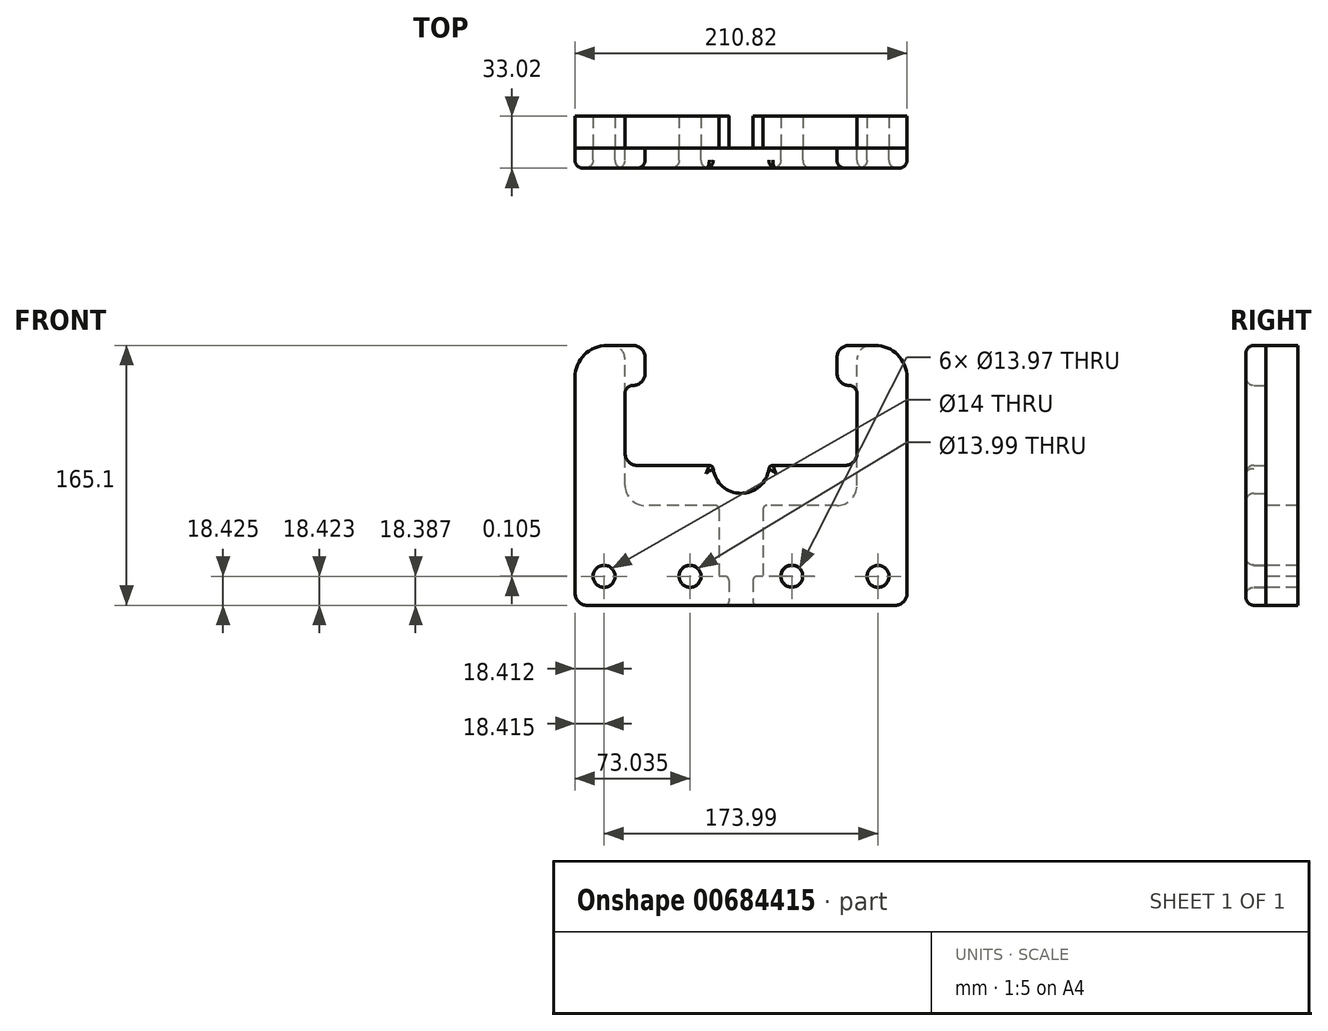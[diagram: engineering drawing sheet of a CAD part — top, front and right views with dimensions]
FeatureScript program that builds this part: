
annotation { "Feature Type Name" : "Feature", "Feature Type Description" : "" }
export const myFeature = defineFeature(function(context is Context, id is Id, definition is map)
    precondition{}
    {
        {
            var Q0;
            Q0=qCreatedBy(makeId("Front.planeOp"),FACE);
            var sketch = newSketch(context, id + "F0", { "sketchPlane" : qUnion([Q0])});
            skLineSegment(sketch, "E0.bottom", {"start": v(53.34, -100.21) * mm, "end": v(8.89, -100.21) * mm});
            skLineSegment(sketch, "E0.left", {"start": v(66.04, -87.51) * mm, "end": v(66.04, -7.5) * mm});
            skLineSegment(sketch, "E0.right", {"start": v(-81.28, -87.51) * mm, "end": v(-81.28, -7.5) * mm});
            skPoint(sketch, "E0.middle", {"position": v(-7.62, 44.57) * mm});
            skPoint(sketch, "E1.visualSharp", {"position": v(-81.28, -100.21) * mm});
            skArc(sketch, "E1.filletArc", {"start": v(-81.28, -87.51) * mm, "mid": v(-77.56, -96.5) * mm, "end": v(-68.58, -100.21) * mm});
            skPoint(sketch, "E2.visualSharp", {"position": v(66.04, -100.21) * mm});
            skArc(sketch, "E2.filletArc", {"start": v(53.34, -100.21) * mm, "mid": v(62.32, -96.5) * mm, "end": v(66.04, -87.51) * mm});
            skPoint(sketch, "E3.visualSharp", {"position": v(66.04, 189.35) * mm});
            skPoint(sketch, "E4.visualSharp", {"position": v(-81.28, 189.35) * mm});
            skLineSegment(sketch, "E5", {"start": v(-92.71, 1.39) * mm, "end": v(-90.17, 1.39) * mm});
            skLineSegment(sketch, "E6", {"start": v(-113.03, -18.93) * mm, "end": v(-113.03, -156.1) * mm});
            skLineSegment(sketch, "E7", {"start": v(97.79, -18.93) * mm, "end": v(97.79, -156.1) * mm});
            skLineSegment(sketch, "E8", {"start": v(-105.41, -163.71) * mm, "end": v(-17.78, -163.71) * mm});
            skLineSegment(sketch, "E9.trimOffspring", {"start": v(74.93, 1.39) * mm, "end": v(77.47, 1.39) * mm});
            skPoint(sketch, "E10.visualSharp", {"position": v(-113.03, 1.39) * mm});
            skArc(sketch, "E10.filletArc", {"start": v(-92.71, 1.39) * mm, "mid": v(-107.08, -4.57) * mm, "end": v(-113.03, -18.93) * mm});
            skPoint(sketch, "E11.visualSharp", {"position": v(-81.28, 1.39) * mm});
            skArc(sketch, "E11.filletArc", {"start": v(-81.28, -7.5) * mm, "mid": v(-83.88, -1.22) * mm, "end": v(-90.17, 1.39) * mm});
            skPoint(sketch, "E12.visualSharp", {"position": v(66.04, 1.39) * mm});
            skArc(sketch, "E12.filletArc", {"start": v(74.93, 1.39) * mm, "mid": v(68.64, -1.22) * mm, "end": v(66.04, -7.5) * mm});
            skPoint(sketch, "E13.visualSharp", {"position": v(97.79, 1.39) * mm});
            skArc(sketch, "E13.filletArc", {"start": v(97.79, -18.93) * mm, "mid": v(91.84, -4.57) * mm, "end": v(77.47, 1.39) * mm});
            skLineSegment(sketch, "E14", {"start": v(-21.6, -100.21) * mm, "end": v(-21.6, -145.3) * mm});
            skLineSegment(sketch, "E15", {"start": v(-21.6, -145.3) * mm, "end": v(-21.6, -102.75) * mm});
            skLineSegment(sketch, "E16", {"start": v(6.35, -102.75) * mm, "end": v(6.35, -145.3) * mm});
            skLineSegment(sketch, "E17", {"start": v(6.35, -145.3) * mm, "end": v(2.54, -145.3) * mm});
            skLineSegment(sketch, "E18", {"start": v(0, -147.84) * mm, "end": v(0, -161.17) * mm});
            skLineSegment(sketch, "E19", {"start": v(0, -163.71) * mm, "end": v(0, -147.84) * mm});
            skLineSegment(sketch, "E20", {"start": v(-15.24, -147.84) * mm, "end": v(-15.24, -161.17) * mm});
            skLineSegment(sketch, "E21.trimOffspring", {"start": v(-24.13, -100.21) * mm, "end": v(-68.58, -100.21) * mm});
            skPoint(sketch, "E22.visualSharp", {"position": v(-21.6, -100.21) * mm});
            skArc(sketch, "E22.filletArc", {"start": v(-21.6, -102.75) * mm, "mid": v(-22.33, -100.96) * mm, "end": v(-24.13, -100.21) * mm});
            skPoint(sketch, "E23.visualSharp", {"position": v(6.35, -100.21) * mm});
            skArc(sketch, "E23.filletArc", {"start": v(8.89, -100.21) * mm, "mid": v(7.1, -100.96) * mm, "end": v(6.35, -102.75) * mm});
            skLineSegment(sketch, "E24.trimOffspring", {"start": v(-17.78, -145.3) * mm, "end": v(-21.6, -145.3) * mm});
            skLineSegment(sketch, "E25.trimOffspring", {"start": v(2.54, -163.71) * mm, "end": v(90.17, -163.71) * mm});
            skPoint(sketch, "E26.visualSharp", {"position": v(-15.24, -145.3) * mm});
            skArc(sketch, "E26.filletArc", {"start": v(-15.24, -147.84) * mm, "mid": v(-15.98, -146.04) * mm, "end": v(-17.78, -145.3) * mm});
            skPoint(sketch, "E27.visualSharp", {"position": v(0, -145.3) * mm});
            skArc(sketch, "E27.filletArc", {"start": v(2.54, -145.3) * mm, "mid": v(0.74, -146.04) * mm, "end": v(0, -147.84) * mm});
            skPoint(sketch, "E28.visualSharp", {"position": v(0, -163.71) * mm});
            skArc(sketch, "E28.filletArc", {"start": v(0, -161.17) * mm, "mid": v(0.74, -162.97) * mm, "end": v(2.54, -163.71) * mm});
            skPoint(sketch, "E29.visualSharp", {"position": v(-15.24, -163.71) * mm});
            skArc(sketch, "E29.filletArc", {"start": v(-17.78, -163.71) * mm, "mid": v(-15.98, -162.97) * mm, "end": v(-15.24, -161.17) * mm});
            skLineSegment(sketch, "E30", {"start": v(-21.6, -145.3) * mm, "end": v(-17.78, -145.3) * mm});
            skCircle(sketch, "E31", {"center": v(-94.62, -145.3) * mm, "radius": 6.99 * mm});
            skCircle(sketch, "E32", {"center": v(-40, -145.3) * mm, "radius": 6.99 * mm});
            skCircle(sketch, "E33", {"center": v(24.76, -145.3) * mm, "radius": 6.99 * mm});
            skCircle(sketch, "E34", {"center": v(79.37, -145.3) * mm, "radius": 6.99 * mm});
            skPoint(sketch, "E35.orphan", {"position": v(-113.03, -145.3) * mm});
            skPoint(sketch, "E36.trimOffspring.end.orphan", {"position": v(-94.62, -163.71) * mm});
            skPoint(sketch, "E37.start.orphan", {"position": v(-40, -163.71) * mm});
            skLineSegment(sketch, "E38.trimOffspring", {"start": v(2.54, -145.3) * mm, "end": v(6.35, -145.3) * mm});
            skPoint(sketch, "E39.start.orphan", {"position": v(24.77, -163.71) * mm});
            skPoint(sketch, "E40.orphan", {"position": v(79.37, -163.71) * mm});
            skPoint(sketch, "E41.visualSharp", {"position": v(-113.03, -163.71) * mm});
            skArc(sketch, "E41.filletArc", {"start": v(-113.03, -156.1) * mm, "mid": v(-110.8, -161.48) * mm, "end": v(-105.41, -163.71) * mm});
            skPoint(sketch, "E42.visualSharp", {"position": v(97.79, -163.71) * mm});
            skArc(sketch, "E42.filletArc", {"start": v(90.17, -163.71) * mm, "mid": v(95.56, -161.48) * mm, "end": v(97.79, -156.1) * mm});
            skSolve(sketch);
        }
        {
            var Q0;
            Q0=makeQuery(id+"F0.imprint","IMPRINT",FACE,{"disambiguationData":[TD([[makeQuery(id+"F0.imprint","IMPRINT",EDGE,{"derivedFrom":sQuery(id+"F0.wireOp",EDGE,"E0.right")}),1.0]])]});
            var sketch = newSketch(context, id + "F1", { "sketchPlane" : qUnion([Q0])});
            skLineSegment(sketch, "E43.0", {"start": v(-81.28, -67.2) * mm, "end": v(-81.28, -29.1) * mm});
            skArc(sketch, "E43.7", {"start": v(-92.71, 1.39) * mm, "mid": v(-107.08, -4.57) * mm, "end": v(-113.03, -18.93) * mm});
            skLineSegment(sketch, "E43.8", {"start": v(-113.03, -18.93) * mm, "end": v(-113.03, -156.1) * mm});
            skLineSegment(sketch, "E43.9", {"start": v(-105.41, -163.71) * mm, "end": v(-15.24, -163.71) * mm});
            skArc(sketch, "E44.1", {"start": v(97.79, -18.93) * mm, "mid": v(91.84, -4.57) * mm, "end": v(77.47, 1.39) * mm});
            skLineSegment(sketch, "E44.2", {"start": v(97.79, -156.1) * mm, "end": v(97.79, -18.93) * mm});
            skLineSegment(sketch, "E44.3", {"start": v(0, -163.71) * mm, "end": v(90.17, -163.71) * mm});
            skLineSegment(sketch, "E44.6", {"start": v(66.04, -29.1) * mm, "end": v(66.04, -67.2) * mm});
            skLineSegment(sketch, "E45", {"start": v(-56.44, -74.81) * mm, "end": v(-27.78, -74.81) * mm});
            skLineSegment(sketch, "E46", {"start": v(-56.44, -74.81) * mm, "end": v(-73.66, -74.81) * mm});
            skLineSegment(sketch, "E47", {"start": v(-15.24, -163.71) * mm, "end": v(0, -163.71) * mm});
            skPoint(sketch, "E48.orphan", {"position": v(-58.21, 0) * mm});
            skLineSegment(sketch, "E49", {"start": v(-92.71, 1.39) * mm, "end": v(-76.2, 1.39) * mm});
            skLineSegment(sketch, "E50", {"start": v(77.47, 1.39) * mm, "end": v(60.96, 1.39) * mm});
            skLineSegment(sketch, "E51", {"start": v(-68.58, -6.23) * mm, "end": v(-68.58, -16.4) * mm});
            skLineSegment(sketch, "E52", {"start": v(53.34, -6.23) * mm, "end": v(53.34, -16.4) * mm});
            skLineSegment(sketch, "E53", {"start": v(60.96, -24.01) * mm, "end": v(60.96, -24.01) * mm});
            skLineSegment(sketch, "E54", {"start": v(-76.2, -24.01) * mm, "end": v(-76.2, -24.01) * mm});
            skPoint(sketch, "E55.visualSharp", {"position": v(-68.58, 1.39) * mm});
            skArc(sketch, "E55.filletArc", {"start": v(-68.58, -6.23) * mm, "mid": v(-70.81, -0.85) * mm, "end": v(-76.2, 1.39) * mm});
            skPoint(sketch, "E56.visualSharp", {"position": v(-68.58, -24.01) * mm});
            skArc(sketch, "E56.filletArc", {"start": v(-76.2, -24.01) * mm, "mid": v(-70.81, -21.78) * mm, "end": v(-68.58, -16.4) * mm});
            skPoint(sketch, "E57.newPointB", {"position": v(-81.28, -7.5) * mm});
            skArc(sketch, "E57.filletArc", {"start": v(-76.2, -24.01) * mm, "mid": v(-79.8, -25.5) * mm, "end": v(-81.28, -29.1) * mm});
            skPoint(sketch, "E58.visualSharp", {"position": v(53.34, 1.39) * mm});
            skArc(sketch, "E58.filletArc", {"start": v(60.96, 1.39) * mm, "mid": v(55.57, -0.85) * mm, "end": v(53.34, -6.23) * mm});
            skPoint(sketch, "E59.orphan", {"position": v(66.04, -7.5) * mm});
            skPoint(sketch, "E60.visualSharp", {"position": v(53.34, -24.01) * mm});
            skArc(sketch, "E60.filletArc", {"start": v(53.34, -16.4) * mm, "mid": v(55.57, -21.78) * mm, "end": v(60.96, -24.01) * mm});
            skPoint(sketch, "E61.visualSharp", {"position": v(66.04, -24.01) * mm});
            skArc(sketch, "E61.filletArc", {"start": v(66.04, -29.1) * mm, "mid": v(64.55, -25.5) * mm, "end": v(60.96, -24.01) * mm});
            skPoint(sketch, "E62.visualSharp", {"position": v(-81.28, -74.81) * mm});
            skArc(sketch, "E62.filletArc", {"start": v(-81.28, -67.2) * mm, "mid": v(-79.05, -72.58) * mm, "end": v(-73.66, -74.81) * mm});
            skPoint(sketch, "E63.visualSharp", {"position": v(66.04, -74.81) * mm});
            skArc(sketch, "E63.filletArc", {"start": v(58.42, -74.81) * mm, "mid": v(63.8, -72.58) * mm, "end": v(66.04, -67.2) * mm});
            skPoint(sketch, "E64", {"position": v(-7.62, -74.81) * mm});
            skArc(sketch, "E65", {"start": v(-25.26, -77.04) * mm, "mid": v(-7.62, -92.6) * mm, "end": v(10.02, -77.04) * mm});
            skLineSegment(sketch, "E66.trimOffspring", {"start": v(12.54, -74.81) * mm, "end": v(58.42, -74.81) * mm});
            skPoint(sketch, "E67.visualSharp", {"position": v(-25.4, -74.81) * mm});
            skArc(sketch, "E67.filletArc", {"start": v(-25.26, -77.04) * mm, "mid": v(-26.1, -75.45) * mm, "end": v(-27.78, -74.81) * mm});
            skPoint(sketch, "E68.visualSharp", {"position": v(10.16, -74.81) * mm});
            skArc(sketch, "E68.filletArc", {"start": v(12.54, -74.81) * mm, "mid": v(10.86, -75.45) * mm, "end": v(10.02, -77.04) * mm});
            skPoint(sketch, "E69.visualSharp", {"position": v(-113.03, -163.71) * mm});
            skArc(sketch, "E69.filletArc", {"start": v(-113.03, -156.1) * mm, "mid": v(-110.8, -161.48) * mm, "end": v(-105.41, -163.71) * mm});
            skPoint(sketch, "E70.visualSharp", {"position": v(97.79, -163.71) * mm});
            skArc(sketch, "E70.filletArc", {"start": v(90.17, -163.71) * mm, "mid": v(95.56, -161.48) * mm, "end": v(97.79, -156.1) * mm});
            skCircle(sketch, "E71", {"center": v(24.62, -145.22) * mm, "radius": 6.99 * mm});
            skCircle(sketch, "E72", {"center": v(79.37, -145.32) * mm, "radius": 6.99 * mm});
            skCircle(sketch, "E73", {"center": v(-94.62, -145.29) * mm, "radius": 7 * mm});
            skCircle(sketch, "E74", {"center": v(-40, -145.28) * mm, "radius": 7 * mm});
            skSolve(sketch);
        }
        {
            var Q0;
            Q0 = qSketchRegion(id + "F0", true);
            extrude(context, id + "F2", {"entities" : qUnion([Q0]), "depth" : -20.32 * mm, "offsetDistance" : 25.4 * mm});
        }
        {
            var Q0;
            Q0 = qSketchRegion(id + "F1", true);
            extrude(context, id + "F3", {"entities" : qUnion([Q0]), "depth" : 12.7 * mm, "offsetDistance" : 25.4 * mm});
        }
        {
            var Q0;
            Q0=makeQuery(id+"F3.opExtrude","CAP_FACE",FACE,{"disambiguationData":[OSD([sQuery(id+"F1.wireOp",EDGE,"E43.0"),sQuery(id+"F1.wireOp",EDGE,"E43.7"),sQuery(id+"F1.wireOp",EDGE,"E43.8"),sQuery(id+"F1.wireOp",EDGE,"E43.9"),sQuery(id+"F1.wireOp",EDGE,"E44.1"),sQuery(id+"F1.wireOp",EDGE,"E44.2"),sQuery(id+"F1.wireOp",EDGE,"E44.3"),sQuery(id+"F1.wireOp",EDGE,"E44.6"),sQuery(id+"F1.wireOp",EDGE,"E45"),sQuery(id+"F1.wireOp",EDGE,"E46"),sQuery(id+"F1.wireOp",EDGE,"E47"),sQuery(id+"F1.wireOp",EDGE,"E49"),sQuery(id+"F1.wireOp",EDGE,"E50"),sQuery(id+"F1.wireOp",EDGE,"E51"),sQuery(id+"F1.wireOp",EDGE,"E52"),sQuery(id+"F1.wireOp",EDGE,"E55.filletArc"),sQuery(id+"F1.wireOp",EDGE,"E56.filletArc"),sQuery(id+"F1.wireOp",EDGE,"E57.filletArc"),sQuery(id+"F1.wireOp",EDGE,"E58.filletArc"),sQuery(id+"F1.wireOp",EDGE,"E60.filletArc"),sQuery(id+"F1.wireOp",EDGE,"E61.filletArc"),sQuery(id+"F1.wireOp",EDGE,"E62.filletArc"),sQuery(id+"F1.wireOp",EDGE,"E63.filletArc"),sQuery(id+"F1.wireOp",EDGE,"E65"),sQuery(id+"F1.wireOp",EDGE,"E66.trimOffspring"),sQuery(id+"F1.wireOp",EDGE,"E67.filletArc"),sQuery(id+"F1.wireOp",EDGE,"E68.filletArc"),sQuery(id+"F1.wireOp",EDGE,"E69.filletArc"),sQuery(id+"F1.wireOp",EDGE,"E70.filletArc"),sQuery(id+"F1.wireOp",EDGE,"E71"),sQuery(id+"F1.wireOp",EDGE,"E72"),sQuery(id+"F1.wireOp",EDGE,"E73"),sQuery(id+"F1.wireOp",EDGE,"E74")])],"isStart":false});
            fillet(context, id + "F4", {"entities" : qUnion([Q0]), "radius" : 5.08 * mm, "tangentPropagation" : true, "allowEdgeOverflow" : false});
        }
    });
